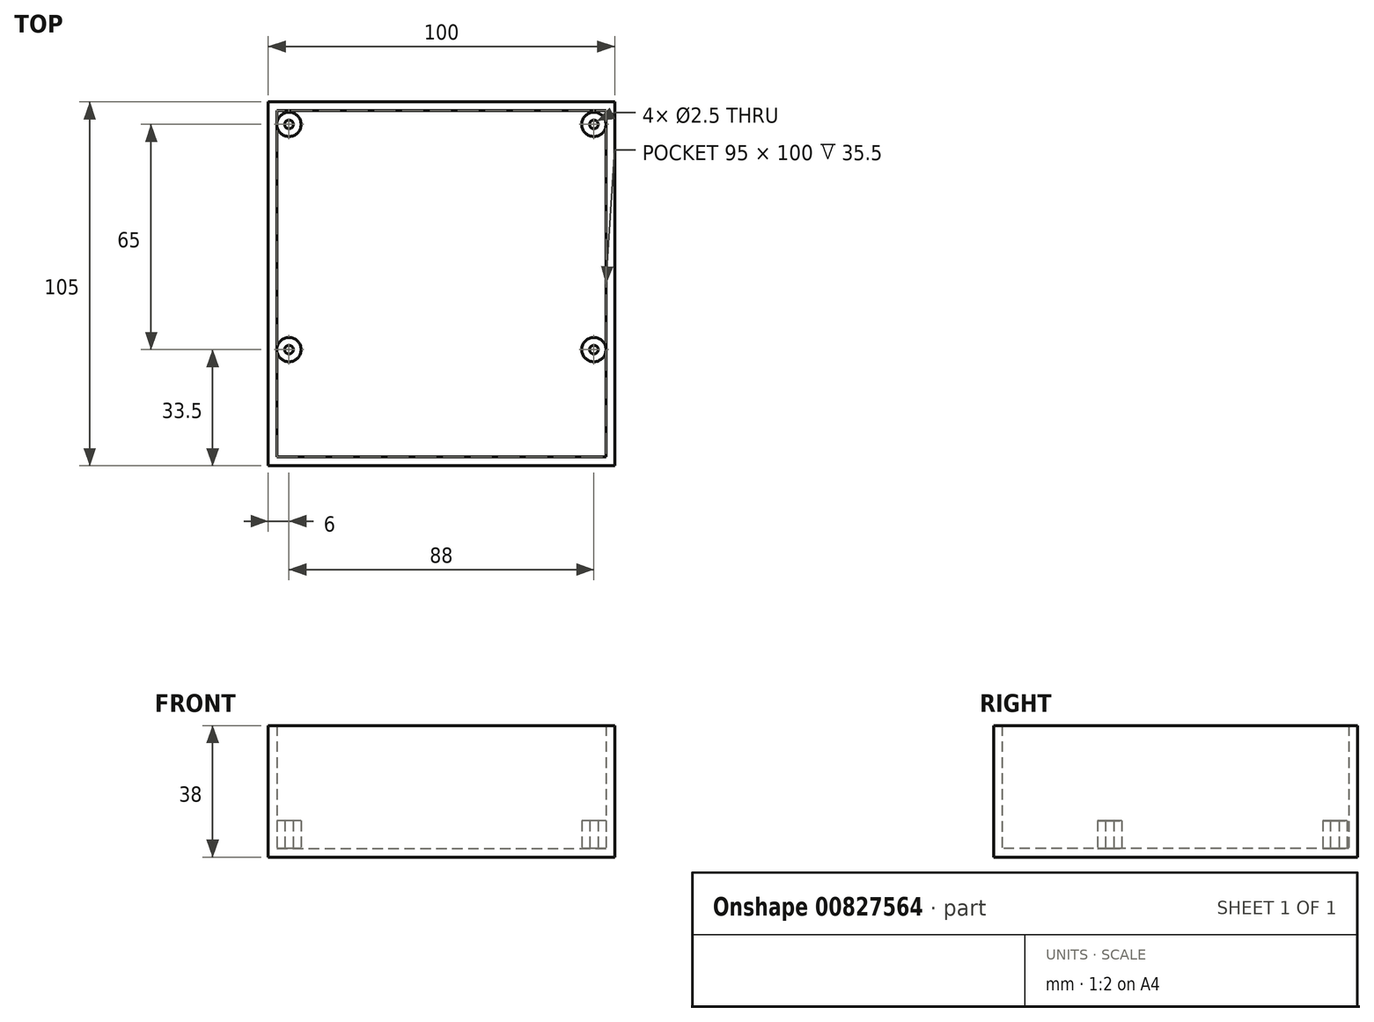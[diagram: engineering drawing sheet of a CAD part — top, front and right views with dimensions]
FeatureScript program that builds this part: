
annotation { "Feature Type Name" : "Feature", "Feature Type Description" : "" }
export const myFeature = defineFeature(function(context is Context, id is Id, definition is map)
    precondition{}
    {
        {
            var Q0;
            Q0=qCreatedBy(makeId("Top.planeOp"),FACE);
            var sketch = newSketch(context, id + "F0", { "sketchPlane" : qUnion([Q0])});
            skLineSegment(sketch, "E0.bottom", {"start": v(-50, 45) * mm, "end": v(50, 45) * mm});
            skLineSegment(sketch, "E0.left", {"start": v(-50, 45) * mm, "end": v(-50, -60) * mm});
            skLineSegment(sketch, "E0.right", {"start": v(50, 45) * mm, "end": v(50, -60) * mm});
            skPoint(sketch, "E0.middle", {"position": v(0, 0) * mm});
            skLineSegment(sketch, "E1.0", {"start": v(-50, -60) * mm, "end": v(50, -60) * mm});
            skPoint(sketch, "E0.top.end.orphan", {"position": v(50, -45) * mm});
            skPoint(sketch, "E0.top.start.orphan", {"position": v(-50, -45) * mm});
            skSolve(sketch);
        }
        {
            var Q0;
            Q0=makeQuery(id+"F0.imprint","IMPRINT",FACE,{"disambiguationData":[TD([[makeQuery(id+"F0.imprint","IMPRINT",EDGE,{"derivedFrom":sQuery(id+"F0.wireOp",EDGE,"E0.bottom")}),-1.0]])]});
            extrude(context, id + "F1", {"entities" : qUnion([Q0]), "depth" : 38 * mm, "offsetDistance" : 25 * mm});
        }
        {
            var Q0;
            Q0=makeQuery(id+"F1.opExtrude","CAP_FACE",FACE,{"disambiguationData":[OSD([sQuery(id+"F0.wireOp",EDGE,"E0.bottom"),sQuery(id+"F0.wireOp",EDGE,"E0.top"),sQuery(id+"F0.wireOp",EDGE,"E0.left"),sQuery(id+"F0.wireOp",EDGE,"E0.right")])],"isStart":false});
            shell(context, id + "F2", {"entities" : qUnion([Q0]), "thickness" : 2.5 * mm});
        }
        {
            var Q0;
            Q0=makeQuery(id+"F2.opShell","OFFSET_FACE",FACE,{"disambiguationData":[OSD([sQuery(id+"F0.wireOp",EDGE,"E0.bottom"),sQuery(id+"F0.wireOp",EDGE,"E0.top"),sQuery(id+"F0.wireOp",EDGE,"E0.left"),sQuery(id+"F0.wireOp",EDGE,"E0.right")])]});
            cPlane(context, id + "F3", {"entities" : qUnion([Q0]), "cplaneType" : CPlaneType.OFFSET, "offset" : 0 * mm, "width" : 150 * mm, "height" : 150 * mm});
        }
        {
            var Q0;
            Q0=qCreatedBy(id+"F3.planeOp",FACE);
            var sketch = newSketch(context, id + "F4", { "sketchPlane" : qUnion([Q0])});
            skLineSegment(sketch, "E2.bottom", {"start": v(-44, 38.5) * mm, "end": v(44, 38.5) * mm, "construction": true});
            skLineSegment(sketch, "E2.top", {"start": v(-44, -26.5) * mm, "end": v(44, -26.5) * mm, "construction": true});
            skLineSegment(sketch, "E2.left", {"start": v(-44, 38.5) * mm, "end": v(-44, -26.5) * mm, "construction": true});
            skLineSegment(sketch, "E2.right", {"start": v(44, 38.5) * mm, "end": v(44, -26.5) * mm, "construction": true});
            skPoint(sketch, "E2.middle", {"position": v(0, 6) * mm});
            skCircle(sketch, "E3", {"center": v(-44, 38.5) * mm, "radius": 3.5 * mm});
            skCircle(sketch, "E4", {"center": v(44, 38.5) * mm, "radius": 3.5 * mm});
            skCircle(sketch, "E5", {"center": v(44, -26.5) * mm, "radius": 3.5 * mm});
            skCircle(sketch, "E6", {"center": v(-44, -26.5) * mm, "radius": 3.5 * mm});
            skCircle(sketch, "E7", {"center": v(-44, 38.5) * mm, "radius": 1.25 * mm});
            skCircle(sketch, "E8", {"center": v(44, 38.5) * mm, "radius": 1.25 * mm});
            skCircle(sketch, "E9", {"center": v(44, -26.5) * mm, "radius": 1.25 * mm});
            skCircle(sketch, "E10", {"center": v(-44, -26.5) * mm, "radius": 1.25 * mm});
            skSolve(sketch);
        }
        {
            var Q0;
            Q0=makeQuery(id+"F4.imprint","IMPRINT",FACE,{"disambiguationData":[TD([[makeQuery(id+"F4.imprint","IMPRINT",EDGE,{"derivedFrom":sQuery(id+"F4.wireOp",EDGE,"E4")}),1.0]])]});
            var Q1;
            Q1=makeQuery(id+"F4.imprint","IMPRINT",FACE,{"disambiguationData":[TD([[makeQuery(id+"F4.imprint","IMPRINT",EDGE,{"derivedFrom":sQuery(id+"F4.wireOp",EDGE,"E3")}),1.0]])]});
            var Q2;
            Q2=makeQuery(id+"F4.imprint","IMPRINT",FACE,{"disambiguationData":[TD([[makeQuery(id+"F4.imprint","IMPRINT",EDGE,{"derivedFrom":sQuery(id+"F4.wireOp",EDGE,"E6")}),1.0]])]});
            var Q3;
            Q3=makeQuery(id+"F4.imprint","IMPRINT",FACE,{"disambiguationData":[TD([[makeQuery(id+"F4.imprint","IMPRINT",EDGE,{"derivedFrom":sQuery(id+"F4.wireOp",EDGE,"E5")}),1.0]])]});
            extrude(context, id + "F5", {"entities" : qUnion([Q0, Q1, Q2, Q3]), "depth" : 8 * mm, "offsetDistance" : 25 * mm});
        }
    });
